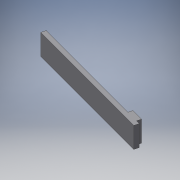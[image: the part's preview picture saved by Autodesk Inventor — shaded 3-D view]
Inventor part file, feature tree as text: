
AUTODESK INVENTOR PART (.ipt)
format: ipt  version: 2016 SP2 (Build 200236200, 236)  size: 98,816 bytes
history: native  units: mm
features: reference x5, extrude x1, sketch x1
ambient origin geometry x8: Origin, YZ Plane, XZ Plane, XY Plane, X Axis, Y Axis, Z Axis, Center Point
bodies: Volumenkörper1 (feature_tree)
feature tree (7):
  extrude  "Extrusion1"  Depth=8.0mm
  sketch  "Skizze1"  dims[d0=51.0mm d2=2.0mm d3=8.0mm d4=0.0mm d5=0.15mm]
  reference  "Referenz1"
  reference  "Referenz2"
  reference  "Referenz3"
  reference  "Referenz4"
  reference  "Referenz5"
